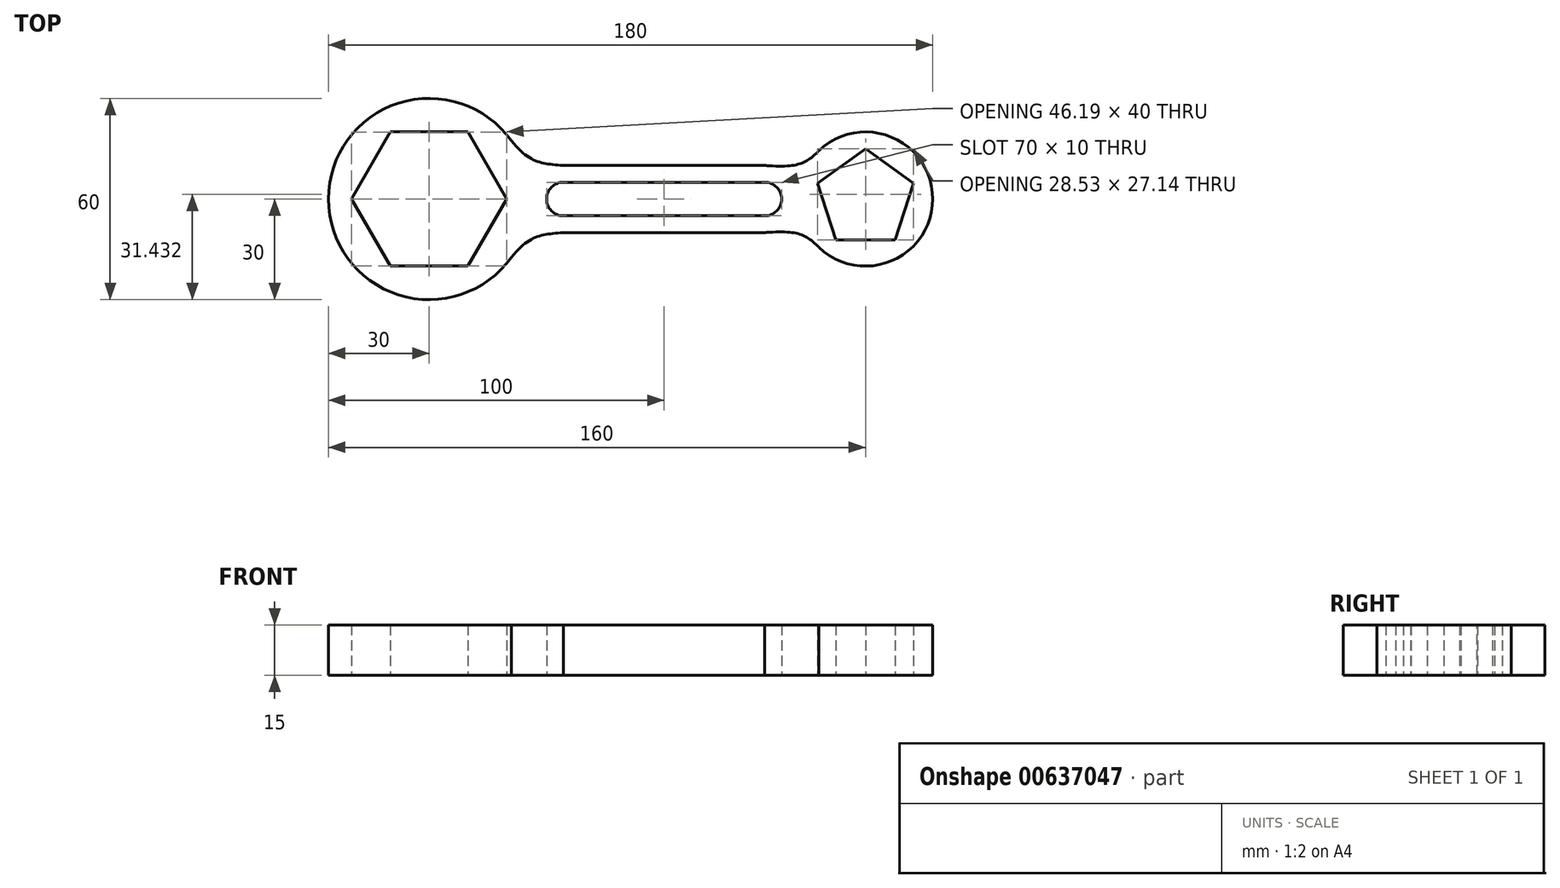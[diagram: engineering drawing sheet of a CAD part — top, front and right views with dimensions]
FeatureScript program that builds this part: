
annotation { "Feature Type Name" : "Feature", "Feature Type Description" : "" }
export const myFeature = defineFeature(function(context is Context, id is Id, definition is map)
    precondition{}
    {
        {
            var Q0;
            Q0=qCreatedBy(makeId("Top.planeOp"),FACE);
            var sketch = newSketch(context, id + "F0", { "sketchPlane" : qUnion([Q0])});
            skLineSegment(sketch, "E0.bottom", {"start": v(-30, -5) * mm, "end": v(30, -5) * mm});
            skLineSegment(sketch, "E0.top", {"start": v(-30, 5) * mm, "end": v(30, 5) * mm});
            skLineSegment(sketch, "E0.left", {"start": v(-30, -5) * mm, "end": v(-30, 5) * mm});
            skLineSegment(sketch, "E0.right", {"start": v(30, -5) * mm, "end": v(30, 5) * mm});
            skArc(sketch, "E1", {"start": v(-30, 5) * mm, "mid": v(-35, 0) * mm, "end": v(-30, -5) * mm});
            skArc(sketch, "E2", {"start": v(30, -5) * mm, "mid": v(35, 0) * mm, "end": v(30, 5) * mm});
            skLineSegment(sketch, "E3.0", {"start": v(-30, 10) * mm, "end": v(30, 10) * mm});
            skArc(sketch, "E3.1", {"start": v(-30, 10) * mm, "mid": v(-40, 0) * mm, "end": v(-30, -10) * mm});
            skLineSegment(sketch, "E3.2", {"start": v(-30, -10) * mm, "end": v(30, -10) * mm});
            skArc(sketch, "E3.3", {"start": v(30, -10) * mm, "mid": v(40, 0) * mm, "end": v(30, 10) * mm});
            skCircle(sketch, "E4", {"center": v(-70, 0) * mm, "radius": 30 * mm});
            skPoint(sketch, "E4.centerSnap0", {"position": v(35, 0) * mm});
            skCircle(sketch, "E5", {"center": v(60, 0) * mm, "radius": 20 * mm});
            skCircle(sketch, "E6.cCircle", {"center": v(-70, 0) * mm, "radius": 20 * mm, "construction": true});
            skLineSegment(sketch, "E6.0", {"start": v(-81.55, 20) * mm, "end": v(-58.45, 20) * mm});
            skLineSegment(sketch, "E6.1", {"start": v(-58.45, 20) * mm, "end": v(-46.9, 0) * mm});
            skLineSegment(sketch, "E6.2", {"start": v(-46.9, 0) * mm, "end": v(-58.45, -20) * mm});
            skLineSegment(sketch, "E6.3", {"start": v(-58.45, -20) * mm, "end": v(-81.55, -20) * mm});
            skLineSegment(sketch, "E6.4", {"start": v(-81.55, -20) * mm, "end": v(-93.1, 0) * mm});
            skLineSegment(sketch, "E6.5", {"start": v(-93.1, 0) * mm, "end": v(-81.55, 20) * mm});
            skPoint(sketch, "E6.0.midPoint", {"position": v(-70, 20) * mm});
            skCircle(sketch, "E7.cCircle", {"center": v(60, 0) * mm, "radius": 12.14 * mm, "construction": true});
            skLineSegment(sketch, "E7.0", {"start": v(60, 15) * mm, "end": v(74.27, 4.64) * mm});
            skLineSegment(sketch, "E7.1", {"start": v(74.27, 4.64) * mm, "end": v(68.82, -12.14) * mm});
            skLineSegment(sketch, "E7.2", {"start": v(68.82, -12.14) * mm, "end": v(51.18, -12.14) * mm});
            skLineSegment(sketch, "E7.3", {"start": v(51.18, -12.14) * mm, "end": v(45.73, 4.64) * mm});
            skLineSegment(sketch, "E7.4", {"start": v(45.73, 4.64) * mm, "end": v(60, 15) * mm});
            skPoint(sketch, "E7.0.midPoint", {"position": v(67.13, 9.82) * mm});
            skFitSpline(sketch, "E8", {"points": [v(-30, 10) * mm, v(-45.53, 17.35) * mm], "startDerivative": vector(-19.7, 1.83) * mm, "endDerivative": vector(-17.4, 20.68) * mm});
            skFitSpline(sketch, "E9.MirrorCS", {"points": [v(-30, -10) * mm, v(-45.53, -17.35) * mm], "startDerivative": vector(-19.7, -1.83) * mm, "endDerivative": vector(-17.4, -20.68) * mm});
            skFitSpline(sketch, "E10", {"points": [v(30, 10) * mm, v(46.13, 14.4) * mm], "startDerivative": vector(28.59, -2) * mm, "endDerivative": vector(12.48, 12.47) * mm});
            skFitSpline(sketch, "E11.MirrorCS", {"points": [v(30, -10) * mm, v(46.13, -14.4) * mm], "startDerivative": vector(28.59, 2) * mm, "endDerivative": vector(12.48, -12.47) * mm});
            skSolve(sketch);
        }
        {
            var Q0;
            Q0=makeQuery(id+"F0.imprint","IMPRINT",FACE,{"disambiguationData":[TD([[makeQuery(id+"F0.imprint","IMPRINT",EDGE,{"derivedFrom":sQuery(id+"F0.wireOp",EDGE,"E6.0")}),1.0]])]});
            var Q1;
            {var subQ0=sQuery(id+"F0.wireOp",EDGE,"E9.MirrorCS");Q1=makeQuery(id+"F0.imprint","IMPRINT",FACE,{"disambiguationData":[TD([[makeQuery(id+"F0.imprint","IMPRINT",EDGE,{"derivedFrom":subQ0}),-1.0]])]});}
            var Q2;
            {var subQ0=sQuery(id+"F0.wireOp",EDGE,"E8");Q2=makeQuery(id+"F0.imprint","IMPRINT",FACE,{"disambiguationData":[TD([[makeQuery(id+"F0.imprint","IMPRINT",EDGE,{"derivedFrom":subQ0}),1.0]])]});}
            var Q3;
            Q3=makeQuery(id+"F0.imprint","IMPRINT",FACE,{"disambiguationData":[TD([[makeQuery(id+"F0.imprint","IMPRINT",EDGE,{"derivedFrom":sQuery(id+"F0.wireOp",EDGE,"E0.bottom")}),-1.0]])]});
            var Q4;
            {var subQ0=sQuery(id+"F0.wireOp",EDGE,"E10");var subQ1=sQuery(id+"F0.wireOp",EDGE,"E3.3");var subQ2=makeQuery(id+"F0.imprint","INTERSECT",VERTEX,{"derivedFrom":[subQ1,subQ0]});Q4=makeQuery(id+"F0.imprint","IMPRINT",FACE,{"disambiguationData":[TD([[makeQuery(id+"F0.imprint","IMPRINT",EDGE,{"disambiguationData":[TD([[subQ2,1.0]])],"derivedFrom":subQ1}),-1.0]])]});}
            var Q5;
            {var subQ0=sQuery(id+"F0.wireOp",EDGE,"E11.MirrorCS");var subQ1=sQuery(id+"F0.wireOp",EDGE,"E3.3");var subQ2=makeQuery(id+"F0.imprint","INTERSECT",VERTEX,{"derivedFrom":[subQ1,subQ0]});Q5=makeQuery(id+"F0.imprint","IMPRINT",FACE,{"disambiguationData":[TD([[makeQuery(id+"F0.imprint","IMPRINT",EDGE,{"disambiguationData":[TD([[subQ2,-1.0]])],"derivedFrom":subQ1}),-1.0]])]});}
            var Q6;
            Q6=makeQuery(id+"F0.imprint","IMPRINT",FACE,{"disambiguationData":[TD([[makeQuery(id+"F0.imprint","IMPRINT",EDGE,{"derivedFrom":sQuery(id+"F0.wireOp",EDGE,"E7.0")}),1.0]])]});
            extrude(context, id + "F1", {"entities" : qUnion([Q0, Q1, Q2, Q3, Q4, Q5, Q6]), "depth" : 15 * mm, "offsetDistance" : 25 * mm});
        }
    });
